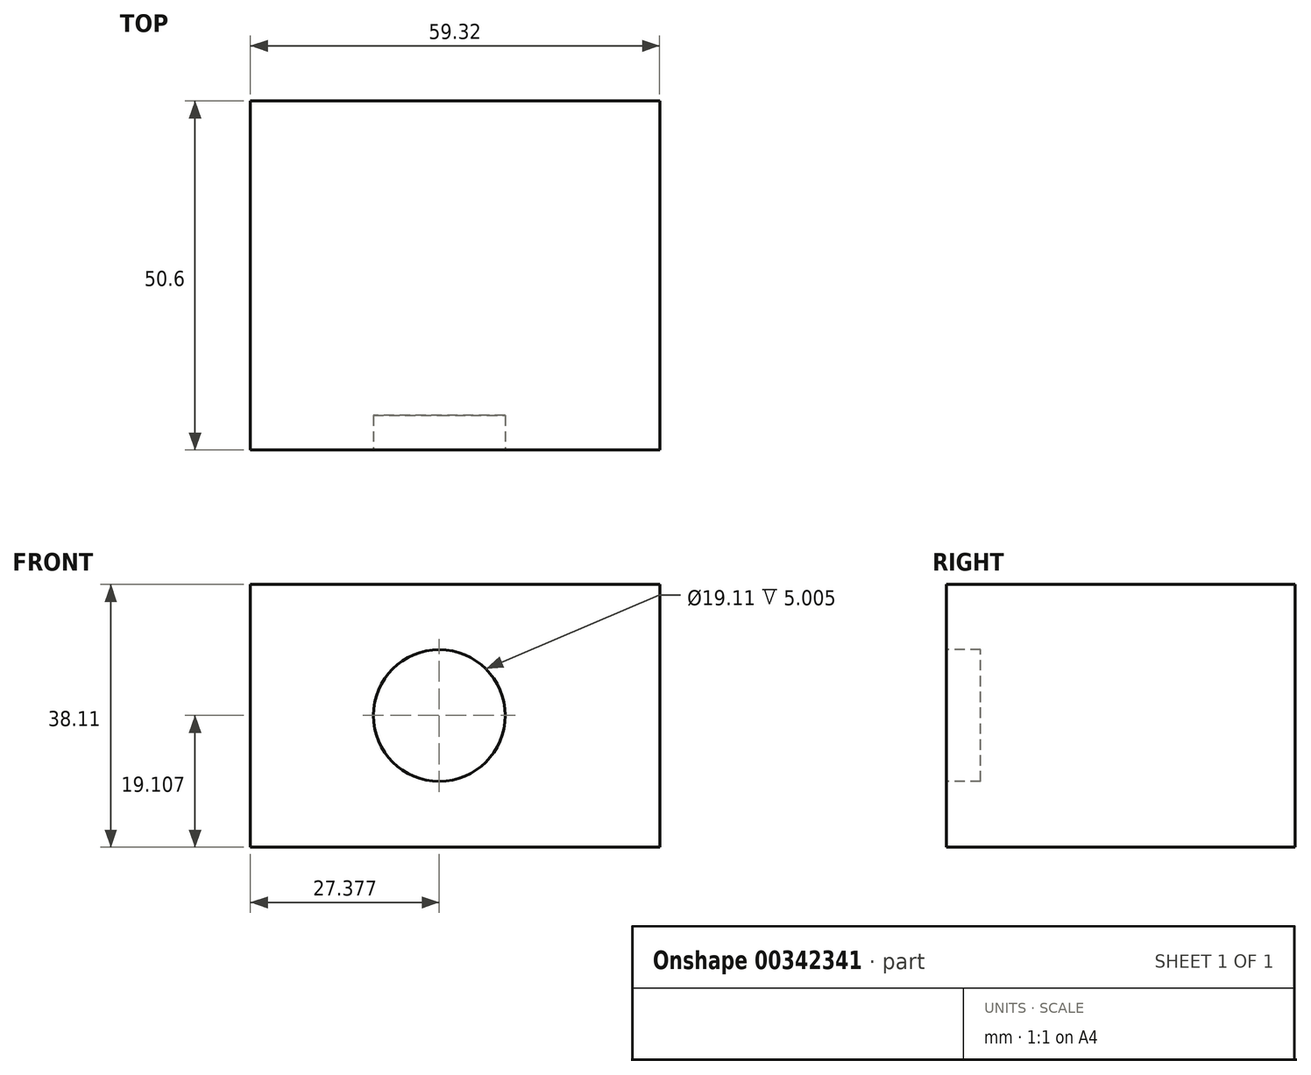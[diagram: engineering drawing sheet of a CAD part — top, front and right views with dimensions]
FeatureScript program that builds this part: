
annotation { "Feature Type Name" : "Feature", "Feature Type Description" : "" }
export const myFeature = defineFeature(function(context is Context, id is Id, definition is map)
    precondition{}
    {
        {
            var Q0;
            Q0=qCreatedBy(makeId("Top.planeOp"),FACE);
            var sketch = newSketch(context, id + "F0", { "sketchPlane" : qUnion([Q0])});
            skLineSegment(sketch, "E0.bottom", {"start": v(29.66, 25.3) * mm, "end": v(-29.66, 25.3) * mm});
            skLineSegment(sketch, "E0.top", {"start": v(29.66, -25.3) * mm, "end": v(-29.66, -25.3) * mm});
            skLineSegment(sketch, "E0.left", {"start": v(29.66, 25.3) * mm, "end": v(29.66, -25.3) * mm});
            skLineSegment(sketch, "E0.right", {"start": v(-29.66, 25.3) * mm, "end": v(-29.66, -25.3) * mm});
            skPoint(sketch, "E0.middle", {"position": v(0, 0) * mm});
            skSolve(sketch);
        }
        {
            var Q0;
            Q0=makeQuery(id+"F0.imprint","IMPRINT",FACE,{"disambiguationData":[TD([[makeQuery(id+"F0.imprint","IMPRINT",EDGE,{"derivedFrom":sQuery(id+"F0.wireOp",EDGE,"E0.bottom")}),1.0]])]});
            extrude(context, id + "F1", {"entities" : qUnion([Q0]), "depth" : 38.1 * mm});
        }
        {
            var Q0;
            Q0=makeQuery(id+"F1.opExtrude","SWEPT_FACE",FACE,{"disambiguationData":[OSD([sQuery(id+"F0.wireOp",EDGE,"E0.top")])]});
            var sketch = newSketch(context, id + "F2", { "sketchPlane" : qUnion([Q0])});
            skCircle(sketch, "E1", {"center": v(-2.28, 19.1) * mm, "radius": 9.56 * mm});
            skSolve(sketch);
        }
        {
            var Q0;
            Q0=makeQuery(id+"F2.imprint","IMPRINT",FACE,{"disambiguationData":[TD([[makeQuery(id+"F2.imprint","IMPRINT",EDGE,{"derivedFrom":sQuery(id+"F2.wireOp",EDGE,"E1")}),1.0]])]});
            extrude(context, id + "F3", {"entities" : qUnion([Q0]), "operationType" : NewBodyOperationType.REMOVE, "oppositeDirection" : true, "depth" : 5 * mm});
        }
    });
